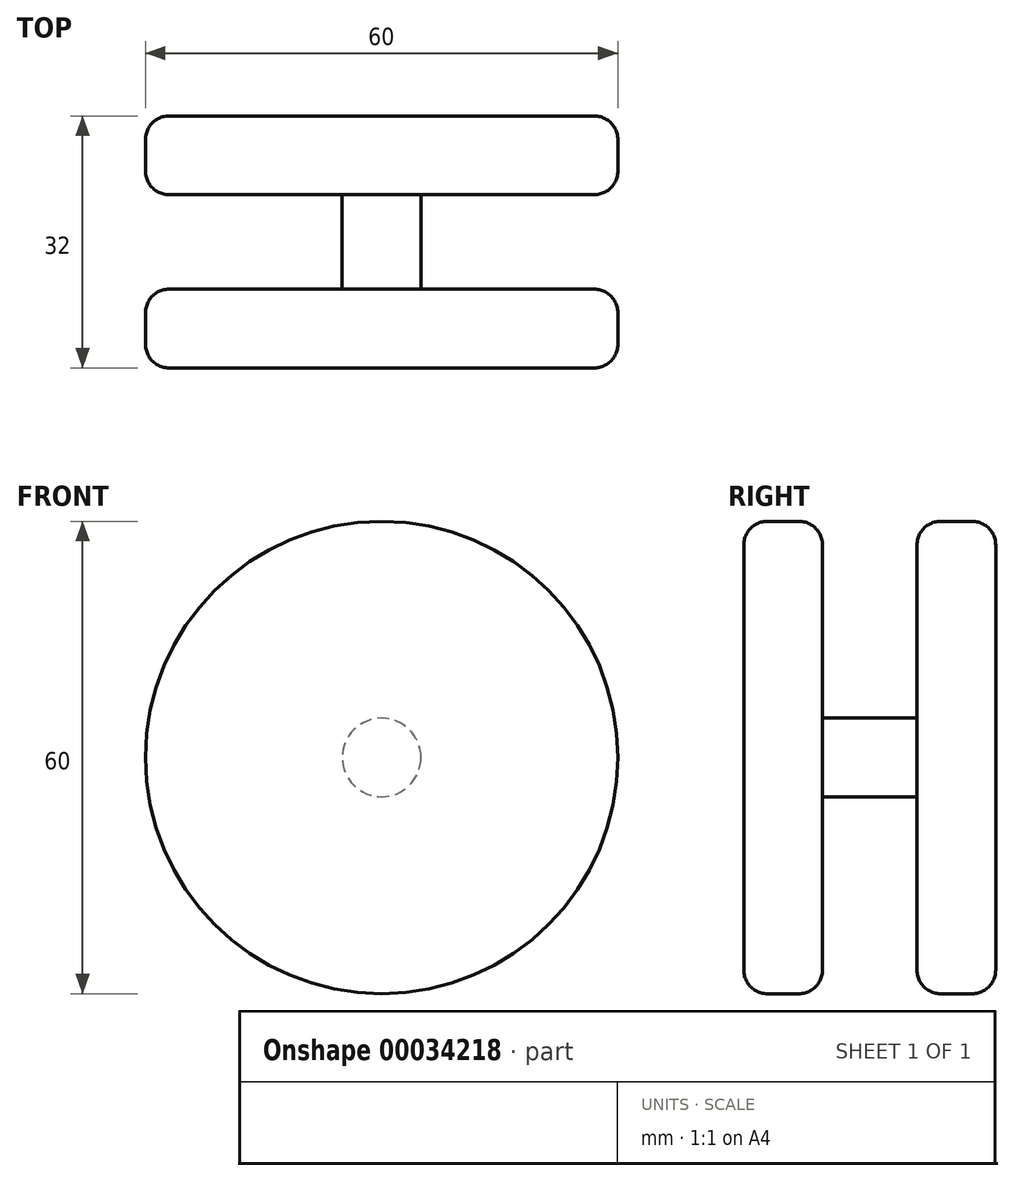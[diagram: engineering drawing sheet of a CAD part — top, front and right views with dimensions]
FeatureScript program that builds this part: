
annotation { "Feature Type Name" : "Feature", "Feature Type Description" : "" }
export const myFeature = defineFeature(function(context is Context, id is Id, definition is map)
    precondition{}
    {
        {
            var Q0;
            Q0=qCreatedBy(makeId("Front.planeOp"),FACE);
            var sketch = newSketch(context, id + "F0", { "sketchPlane" : qUnion([Q0])});
            skCircle(sketch, "E0", {"center": v(0, 0) * mm, "radius": 30 * mm});
            skSolve(sketch);
        }
        {
            var Q0;
            Q0=makeQuery(id+"F0.imprint","IMPRINT",FACE,{"disambiguationData":[TD([[makeQuery(id+"F0.imprint","IMPRINT",EDGE,{"derivedFrom":sQuery(id+"F0.wireOp",EDGE,"E0")}),1.0]])]});
            extrude(context, id + "F1", {"entities" : qUnion([Q0]), "depth" : 10 * mm});
        }
        {
            var Q0;
            Q0=makeQuery(id+"F1.opExtrude","CAP_EDGE",EDGE,{"disambiguationData":[OSD([sQuery(id+"F0.wireOp",EDGE,"E0")])],"isStart":false});
            var Q1;
            Q1=makeQuery(id+"F1.opExtrude","CAP_EDGE",EDGE,{"disambiguationData":[OSD([sQuery(id+"F0.wireOp",EDGE,"E0")])],"isStart":true});
            fillet(context, id + "F2", {"entities" : qUnion([Q0, Q1]), "radius" : 3 * mm, "tangentPropagation" : true, "allowEdgeOverflow" : false});
        }
        {
            var Q0;
            Q0=makeQuery(id+"F1.opExtrude","CAP_FACE",FACE,{"disambiguationData":[OSD([sQuery(id+"F0.wireOp",EDGE,"E0")])],"isStart":false});
            var sketch = newSketch(context, id + "F3", { "sketchPlane" : qUnion([Q0])});
            skCircle(sketch, "E1", {"center": v(0, 0) * mm, "radius": 5 * mm});
            skSolve(sketch);
        }
        {
            var Q0;
            Q0 = qSketchRegion(id + "F3", true);
            var Q1;
            Q1=sQuery(id+"F3.wireOp",EDGE,"E1");
            extrude(context, id + "F4", {"entities" : qUnion([Q0]), "operationType" : NewBodyOperationType.ADD, "surfaceEntities" : qUnion([Q1]), "depth" : 6 * mm});
        }
        {
            var Q0;
            Q0=makeQuery(id+"F1.opExtrude","SWEPT_BODY",BODY,{"disambiguationData":[OSD([sQuery(id+"F0.wireOp",EDGE,"E0")])]});
            var Q1;
            Q1=makeQuery(id+"F4.opExtrude","CAP_FACE",FACE,{"disambiguationData":[OSD([sQuery(id+"F3.wireOp",EDGE,"E1")])],"isStart":false});
            mirror(context, id + "F5", {"operationType" : NewBodyOperationType.ADD, "entities" : qUnion([Q0]), "mirrorPlane" : qUnion([Q1])});
        }
    });
